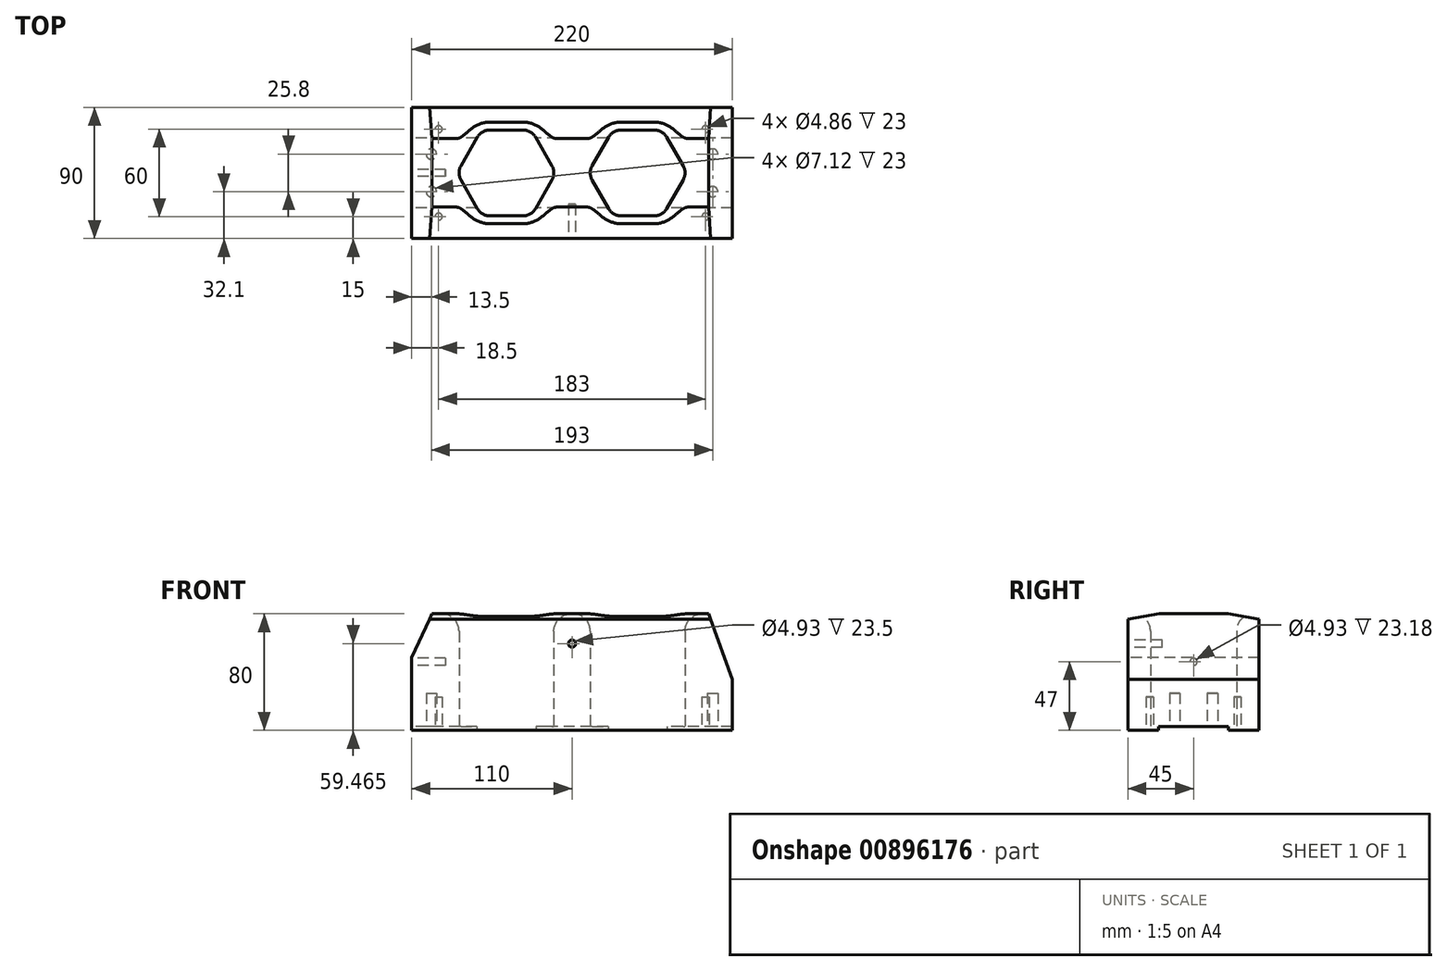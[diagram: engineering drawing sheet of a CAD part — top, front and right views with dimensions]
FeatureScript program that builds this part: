
annotation { "Feature Type Name" : "Feature", "Feature Type Description" : "" }
export const myFeature = defineFeature(function(context is Context, id is Id, definition is map)
    precondition{}
    {
        {
            var Q0;
            Q0=qCreatedBy(makeId("Top.planeOp"),FACE);
            var sketch = newSketch(context, id + "F0", { "sketchPlane" : qUnion([Q0])});
            skLineSegment(sketch, "E0.bottom", {"start": v(110, 45) * mm, "end": v(-110, 45) * mm});
            skLineSegment(sketch, "E0.top", {"start": v(110, -45) * mm, "end": v(-110, -45) * mm});
            skLineSegment(sketch, "E0.left", {"start": v(110, 45) * mm, "end": v(110, -45) * mm});
            skLineSegment(sketch, "E0.right", {"start": v(-110, 45) * mm, "end": v(-110, -45) * mm});
            skPoint(sketch, "E0.middle", {"position": v(0, 0) * mm});
            skSolve(sketch);
        }
        {
            var Q0;
            Q0=makeQuery(id+"F0.imprint","IMPRINT",FACE,{"disambiguationData":[TD([[makeQuery(id+"F0.imprint","IMPRINT",EDGE,{"derivedFrom":sQuery(id+"F0.wireOp",EDGE,"E0.bottom")}),1.0]])]});
            extrude(context, id + "F1", {"entities" : qUnion([Q0]), "depth" : 80 * mm, "offsetDistance" : 25 * mm});
        }
        {
            var Q0;
            {var subQ0=sQuery(id+"F0.wireOp",EDGE,"E0.top");var subQ1=sQuery(id+"F0.wireOp",EDGE,"E0.left");var subQ2=sQuery(id+"F0.wireOp",EDGE,"E0.right");Q0=makeQuery(id+"F8.boolean.opBoolean","SPLIT",FACE,{"disambiguationData":[TD([makeQuery(id+"F1.opExtrude","SWEPT_FACE",FACE,{"disambiguationData":[OSD([subQ0])]})])],"derivedFrom":makeQuery(id+"F1.opExtrude","CAP_FACE",FACE,{"disambiguationData":[OSD([sQuery(id+"F0.wireOp",EDGE,"E0.bottom"),subQ0,subQ1,subQ2])],"isStart":true})});}
            var sketch = newSketch(context, id + "F2", { "sketchPlane" : qUnion([Q0])});
            skLineSegment(sketch, "E1", {"start": v(0, 0) * mm, "end": v(45, 0) * mm});
            skLineSegment(sketch, "E2", {"start": v(0, 0) * mm, "end": v(-45, 0) * mm});
            skLineSegment(sketch, "E3", {"start": v(-45, 0) * mm, "end": v(-45, 29.5) * mm});
            skCircle(sketch, "E4.cCircle", {"center": v(-45, 0) * mm, "radius": 29.5 * mm, "construction": true});
            skLineSegment(sketch, "E4.0", {"start": v(-56.26, 29.5) * mm, "end": v(-33.74, 29.5) * mm});
            skLineSegment(sketch, "E4.1", {"start": v(-25.08, 24.5) * mm, "end": v(-13.82, 5) * mm});
            skLineSegment(sketch, "E4.2", {"start": v(-13.82, -5) * mm, "end": v(-25.08, -24.5) * mm});
            skLineSegment(sketch, "E4.3", {"start": v(-33.74, -29.5) * mm, "end": v(-56.26, -29.5) * mm});
            skLineSegment(sketch, "E4.4", {"start": v(-64.92, -24.5) * mm, "end": v(-76.18, -5) * mm});
            skLineSegment(sketch, "E4.5", {"start": v(-76.18, 5) * mm, "end": v(-64.92, 24.5) * mm});
            skPoint(sketch, "E4.0.midPoint", {"position": v(-45, 29.5) * mm});
            skLineSegment(sketch, "E5", {"start": v(45, 0) * mm, "end": v(45, 29.5) * mm});
            skCircle(sketch, "E6.cCircle", {"center": v(45, 0) * mm, "radius": 29.5 * mm, "construction": true});
            skLineSegment(sketch, "E6.0", {"start": v(33.74, 29.5) * mm, "end": v(56.26, 29.5) * mm});
            skLineSegment(sketch, "E6.1", {"start": v(64.92, 24.5) * mm, "end": v(76.18, 5) * mm});
            skLineSegment(sketch, "E6.2", {"start": v(76.18, -5) * mm, "end": v(64.92, -24.5) * mm});
            skLineSegment(sketch, "E6.3", {"start": v(56.26, -29.5) * mm, "end": v(33.74, -29.5) * mm});
            skLineSegment(sketch, "E6.4", {"start": v(25.08, -24.5) * mm, "end": v(13.82, -5) * mm});
            skLineSegment(sketch, "E6.5", {"start": v(13.82, 5) * mm, "end": v(25.08, 24.5) * mm});
            skPoint(sketch, "E6.0.midPoint", {"position": v(45, 29.5) * mm});
            skPoint(sketch, "E7.visualSharp", {"position": v(-62.03, 29.5) * mm});
            skArc(sketch, "E7.filletArc", {"start": v(-56.26, 29.5) * mm, "mid": v(-61.26, 28.16) * mm, "end": v(-64.92, 24.5) * mm});
            skPoint(sketch, "E8.visualSharp", {"position": v(-79.06, 0) * mm});
            skArc(sketch, "E8.filletArc", {"start": v(-76.18, 5) * mm, "mid": v(-77.52, 0) * mm, "end": v(-76.18, -5) * mm});
            skPoint(sketch, "E9.visualSharp", {"position": v(-62.03, -29.5) * mm});
            skArc(sketch, "E9.filletArc", {"start": v(-64.92, -24.5) * mm, "mid": v(-61.26, -28.16) * mm, "end": v(-56.26, -29.5) * mm});
            skPoint(sketch, "E10.visualSharp", {"position": v(-27.97, -29.5) * mm});
            skArc(sketch, "E10.filletArc", {"start": v(-33.74, -29.5) * mm, "mid": v(-28.74, -28.16) * mm, "end": v(-25.08, -24.5) * mm});
            skPoint(sketch, "E11.visualSharp", {"position": v(-10.94, 0) * mm});
            skArc(sketch, "E11.filletArc", {"start": v(-13.82, -5) * mm, "mid": v(-12.48, 0) * mm, "end": v(-13.82, 5) * mm});
            skPoint(sketch, "E12.visualSharp", {"position": v(-27.97, 29.5) * mm});
            skArc(sketch, "E12.filletArc", {"start": v(-25.08, 24.5) * mm, "mid": v(-28.74, 28.16) * mm, "end": v(-33.74, 29.5) * mm});
            skPoint(sketch, "E13.visualSharp", {"position": v(27.97, 29.5) * mm});
            skArc(sketch, "E13.filletArc", {"start": v(33.74, 29.5) * mm, "mid": v(28.74, 28.16) * mm, "end": v(25.08, 24.5) * mm});
            skPoint(sketch, "E14.visualSharp", {"position": v(10.94, 0) * mm});
            skArc(sketch, "E14.filletArc", {"start": v(13.82, 5) * mm, "mid": v(12.48, 0) * mm, "end": v(13.82, -5) * mm});
            skPoint(sketch, "E15.visualSharp", {"position": v(27.97, -29.5) * mm});
            skArc(sketch, "E15.filletArc", {"start": v(25.08, -24.5) * mm, "mid": v(28.74, -28.16) * mm, "end": v(33.74, -29.5) * mm});
            skPoint(sketch, "E16.visualSharp", {"position": v(62.03, -29.5) * mm});
            skArc(sketch, "E16.filletArc", {"start": v(56.26, -29.5) * mm, "mid": v(61.26, -28.16) * mm, "end": v(64.92, -24.5) * mm});
            skPoint(sketch, "E17.visualSharp", {"position": v(79.06, 0) * mm});
            skArc(sketch, "E17.filletArc", {"start": v(76.18, -5) * mm, "mid": v(77.52, 0) * mm, "end": v(76.18, 5) * mm});
            skPoint(sketch, "E18.visualSharp", {"position": v(62.03, 29.5) * mm});
            skArc(sketch, "E18.filletArc", {"start": v(64.92, 24.5) * mm, "mid": v(61.26, 28.16) * mm, "end": v(56.26, 29.5) * mm});
            skSolve(sketch);
        }
        {
            var Q0;
            {var subQ1=sQuery(id+"F2.wireOp",EDGE,"E4.2");Q0=makeQuery(id+"F2.imprint","IMPRINT",FACE,{"disambiguationData":[TD([[makeQuery(id+"F2.imprint","IMPRINT",EDGE,{"derivedFrom":subQ1}),-1.0]])]});}
            var Q1;
            {var subQ3=sQuery(id+"F2.wireOp",EDGE,"E2");var subQ7=sQuery(id+"F2.wireOp",EDGE,"E3");var subQ8=makeQuery(id+"F2.imprint","INTERSECT",VERTEX,{"derivedFrom":[subQ3,subQ7]});Q1=makeQuery(id+"F2.imprint","IMPRINT",FACE,{"disambiguationData":[TD([[makeQuery(id+"F2.imprint","IMPRINT",EDGE,{"disambiguationData":[TD([[subQ8,1.0]])],"derivedFrom":subQ3}),-1.0]])]});}
            var Q2;
            {var subQ0=sQuery(id+"F2.wireOp",EDGE,"E12.filletArc");Q2=makeQuery(id+"F2.imprint","IMPRINT",FACE,{"disambiguationData":[TD([[makeQuery(id+"F2.imprint","IMPRINT",EDGE,{"derivedFrom":subQ0}),1.0]])]});}
            var Q3;
            {var subQ0=sQuery(id+"F2.wireOp",EDGE,"E7.filletArc");Q3=makeQuery(id+"F2.imprint","IMPRINT",FACE,{"disambiguationData":[TD([[makeQuery(id+"F2.imprint","IMPRINT",EDGE,{"derivedFrom":subQ0}),1.0]])]});}
            var Q4;
            {var subQ0=sQuery(id+"F2.wireOp",EDGE,"E13.filletArc");Q4=makeQuery(id+"F2.imprint","IMPRINT",FACE,{"disambiguationData":[TD([[makeQuery(id+"F2.imprint","IMPRINT",EDGE,{"derivedFrom":subQ0}),1.0]])]});}
            var Q5;
            {var subQ0=sQuery(id+"F2.wireOp",EDGE,"E18.filletArc");Q5=makeQuery(id+"F2.imprint","IMPRINT",FACE,{"disambiguationData":[TD([[makeQuery(id+"F2.imprint","IMPRINT",EDGE,{"derivedFrom":subQ0}),1.0]])]});}
            var Q6;
            Q6=makeQuery(id+"F2.imprint","IMPRINT",FACE,{"disambiguationData":[TD([[makeQuery(id+"F2.imprint","IMPRINT",EDGE,{"derivedFrom":sQuery(id+"F2.wireOp",EDGE,"E6.2")}),-1.0]])]});
            var Q7;
            {var subQ3=sQuery(id+"F2.wireOp",EDGE,"E1");var subQ5=sQuery(id+"F2.wireOp",EDGE,"E5");var subQ6=makeQuery(id+"F2.imprint","INTERSECT",VERTEX,{"derivedFrom":[subQ3,subQ5]});Q7=makeQuery(id+"F2.imprint","IMPRINT",FACE,{"disambiguationData":[TD([[makeQuery(id+"F2.imprint","IMPRINT",EDGE,{"disambiguationData":[TD([[subQ6,1.0]])],"derivedFrom":subQ3}),1.0]])]});}
            extrude(context, id + "F3", {"entities" : qUnion([Q0, Q1, Q2, Q3, Q4, Q5, Q6, Q7]), "operationType" : NewBodyOperationType.REMOVE, "endBound" : BoundingType.THROUGH_ALL, "oppositeDirection" : true, "depth" : 25 * mm, "offsetDistance" : 25 * mm});
        }
        {
            var Q0;
            Q0=makeQuery(id+"F3.boolean.opBoolean","INTERSECT",EDGE,{"derivedFrom":[makeQuery(id+"F1.opExtrude","CAP_FACE",FACE,{"disambiguationData":[OSD([sQuery(id+"F0.wireOp",EDGE,"E0.bottom"),sQuery(id+"F0.wireOp",EDGE,"E0.top"),sQuery(id+"F0.wireOp",EDGE,"E0.left"),sQuery(id+"F0.wireOp",EDGE,"E0.right")])],"isStart":false}),makeQuery(id+"F3.opExtrude","SWEPT_FACE",FACE,{"disambiguationData":[OSD([sQuery(id+"F2.wireOp",EDGE,"E4.3")])]})]});
            var Q1;
            Q1=makeQuery(id+"F3.boolean.opBoolean","INTERSECT",EDGE,{"derivedFrom":[makeQuery(id+"F1.opExtrude","CAP_FACE",FACE,{"disambiguationData":[OSD([sQuery(id+"F0.wireOp",EDGE,"E0.bottom"),sQuery(id+"F0.wireOp",EDGE,"E0.top"),sQuery(id+"F0.wireOp",EDGE,"E0.left"),sQuery(id+"F0.wireOp",EDGE,"E0.right")])],"isStart":false}),makeQuery(id+"F3.opExtrude","SWEPT_FACE",FACE,{"disambiguationData":[OSD([sQuery(id+"F2.wireOp",EDGE,"E6.3")])]})]});
            fillet(context, id + "F4", {"entities" : qUnion([Q0, Q1]), "radius" : 12 * mm, "tangentPropagation" : true, "allowEdgeOverflow" : false});
        }
        {
            var Q0;
            Q0=makeQuery(id+"F1.opExtrude","SWEPT_FACE",FACE,{"disambiguationData":[OSD([sQuery(id+"F0.wireOp",EDGE,"E0.top")])]});
            var sketch = newSketch(context, id + "F5", { "sketchPlane" : qUnion([Q0])});
            skPoint(sketch, "E19.middle", {"position": v(0, 65.95) * mm});
            skPoint(sketch, "E20.orphan", {"position": v(0, 51.9) * mm});
            skPoint(sketch, "E21.end.orphan", {"position": v(0, 80) * mm});
            skPoint(sketch, "E22.top.end.orphan", {"position": v(-95, 50) * mm});
            skPoint(sketch, "E23.trimOffspring.start.orphan", {"position": v(95, 50) * mm});
            skLineSegment(sketch, "E24", {"start": v(-110, 50) * mm, "end": v(-96.01, 80) * mm});
            skLineSegment(sketch, "E25", {"start": v(-110, 80) * mm, "end": v(-110, 50) * mm});
            skLineSegment(sketch, "E26", {"start": v(110, 35) * mm, "end": v(93.62, 80) * mm});
            skLineSegment(sketch, "E27", {"start": v(110, 80) * mm, "end": v(110, 35) * mm});
            skLineSegment(sketch, "E28", {"start": v(0, 0) * mm, "end": v(0, 80) * mm});
            skLineSegment(sketch, "E29", {"start": v(110, 80) * mm, "end": v(93.62, 80) * mm});
            skLineSegment(sketch, "E30", {"start": v(-110, 80) * mm, "end": v(-96.01, 80) * mm});
            skSolve(sketch);
        }
        {
            var Q0;
            Q0=makeQuery(id+"F5.imprint","IMPRINT",FACE,{"disambiguationData":[TD([[makeQuery(id+"F5.imprint","IMPRINT",EDGE,{"derivedFrom":sQuery(id+"F5.wireOp",EDGE,"tVCkyzY6-PQv7-pjYg-ZoG2-eNGS0VEvuOqP")}),-1.0]])]});
            var Q1;
            Q1=makeQuery(id+"F5.imprint","IMPRINT",FACE,{"disambiguationData":[TD([[makeQuery(id+"F5.imprint","IMPRINT",EDGE,{"derivedFrom":sQuery(id+"F5.wireOp",EDGE,"MdysPOFG-TD7O-rCdf-9AqD-u6KUDIQ9QJOj")}),1.0]])]});
            var Q2;
            Q2=makeQuery(id+"F5.imprint","IMPRINT",FACE,{"disambiguationData":[TD([[makeQuery(id+"F5.imprint","IMPRINT",EDGE,{"derivedFrom":sQuery(id+"F5.wireOp",EDGE,"E24")}),1.0]])]});
            var Q3;
            Q3=makeQuery(id+"F5.imprint","IMPRINT",FACE,{"disambiguationData":[TD([[makeQuery(id+"F5.imprint","IMPRINT",EDGE,{"derivedFrom":sQuery(id+"F5.wireOp",EDGE,"E26")}),-1.0]])]});
            extrude(context, id + "F6", {"entities" : qUnion([Q0, Q1, Q2, Q3]), "operationType" : NewBodyOperationType.REMOVE, "oppositeDirection" : true, "depth" : 90 * mm, "offsetDistance" : 25 * mm});
        }
        {
            var Q0;
            Q0=makeQuery(id+"F1.opExtrude","SWEPT_FACE",FACE,{"disambiguationData":[OSD([sQuery(id+"F0.wireOp",EDGE,"E0.right")])]});
            var sketch = newSketch(context, id + "F7", { "sketchPlane" : qUnion([Q0])});
            skLineSegment(sketch, "E31", {"start": v(0, 0) * mm, "end": v(24, 0) * mm});
            skLineSegment(sketch, "E32", {"start": v(24, 0) * mm, "end": v(24, 2.5) * mm});
            skLineSegment(sketch, "E33", {"start": v(24, 2.5) * mm, "end": v(-24, 2.5) * mm});
            skLineSegment(sketch, "E34", {"start": v(-24, 2.5) * mm, "end": v(-24, 0) * mm});
            skLineSegment(sketch, "E35", {"start": v(-24, 0) * mm, "end": v(0, 0) * mm});
            skLineSegment(sketch, "E36", {"start": v(45, 78.17) * mm, "end": v(44.95, 78.17) * mm});
            skPoint(sketch, "E37.orphan", {"position": v(52.39, 80) * mm});
            skLineSegment(sketch, "E38.0", {"start": v(-45, 80) * mm, "end": v(-23.5, 80) * mm});
            skLineSegment(sketch, "E39", {"start": v(45, 76.2) * mm, "end": v(45, 80) * mm});
            skLineSegment(sketch, "E40", {"start": v(-45, 76.2) * mm, "end": v(-45, 80) * mm});
            skPoint(sketch, "E41.orphan", {"position": v(45.33, 80) * mm});
            skLineSegment(sketch, "E42", {"start": v(23.5, 80) * mm, "end": v(45, 76.2) * mm});
            skLineSegment(sketch, "E43", {"start": v(-23.5, 80) * mm, "end": v(-45, 76.2) * mm});
            skLineSegment(sketch, "E44.trimOffspring", {"start": v(23.5, 80) * mm, "end": v(45, 80) * mm});
            skPoint(sketch, "E45.start.orphan", {"position": v(0, 80) * mm});
            skSolve(sketch);
        }
        {
            var Q0;
            Q0=makeQuery(id+"F7.imprint","IMPRINT",FACE,{"disambiguationData":[TD([[makeQuery(id+"F7.imprint","IMPRINT",EDGE,{"derivedFrom":sQuery(id+"F7.wireOp",EDGE,"E38.0")}),-1.0]])]});
            var Q1;
            {var subQ2=sQuery(id+"F7.wireOp",EDGE,"E42");Q1=makeQuery(id+"F7.imprint","IMPRINT",FACE,{"disambiguationData":[TD([[makeQuery(id+"F7.imprint","IMPRINT",EDGE,{"derivedFrom":subQ2}),1.0]])]});}
            var Q2;
            Q2=makeQuery(id+"F7.imprint","IMPRINT",FACE,{"disambiguationData":[TD([[makeQuery(id+"F7.imprint","IMPRINT",EDGE,{"derivedFrom":sQuery(id+"F7.wireOp",EDGE,"E31")}),1.0]])]});
            extrude(context, id + "F8", {"entities" : qUnion([Q0, Q1, Q2]), "operationType" : NewBodyOperationType.REMOVE, "endBound" : BoundingType.THROUGH_ALL, "oppositeDirection" : true, "depth" : 25 * mm, "offsetDistance" : 25 * mm});
        }
        {
            var Q0;
            Q0=makeQuery(id+"F1.opExtrude","SWEPT_FACE",FACE,{"disambiguationData":[OSD([sQuery(id+"F0.wireOp",EDGE,"E0.right")])]});
            var sketch = newSketch(context, id + "F9", { "sketchPlane" : qUnion([Q0])});
            skCircle(sketch, "E46", {"center": v(0, 47) * mm, "radius": 2.46 * mm});
            skSolve(sketch);
        }
        {
            var Q0;
            Q0=makeQuery(id+"F9.imprint","IMPRINT",FACE,{"disambiguationData":[TD([[makeQuery(id+"F9.imprint","IMPRINT",EDGE,{"derivedFrom":sQuery(id+"F9.wireOp",EDGE,"E46")}),1.0]])]});
            extrude(context, id + "F10", {"entities" : qUnion([Q0]), "operationType" : NewBodyOperationType.REMOVE, "oppositeDirection" : true, "depth" : 23.18 * mm, "offsetDistance" : 25 * mm});
        }
        {
            var Q0;
            Q0=makeQuery(id+"F1.opExtrude","SWEPT_FACE",FACE,{"disambiguationData":[OSD([sQuery(id+"F0.wireOp",EDGE,"E0.top")])]});
            var sketch = newSketch(context, id + "F11", { "sketchPlane" : qUnion([Q0])});
            skCircle(sketch, "E47", {"center": v(0, 59.47) * mm, "radius": 2.46 * mm});
            skSolve(sketch);
        }
        {
            var Q0;
            Q0=makeQuery(id+"F11.imprint","IMPRINT",FACE,{"disambiguationData":[TD([[makeQuery(id+"F11.imprint","IMPRINT",EDGE,{"derivedFrom":sQuery(id+"F11.wireOp",EDGE,"E47")}),1.0]])]});
            extrude(context, id + "F12", {"entities" : qUnion([Q0]), "operationType" : NewBodyOperationType.REMOVE, "oppositeDirection" : true, "depth" : 23.5 * mm, "offsetDistance" : 25 * mm});
        }
        {
            var Q0;
            {var subQ0=sQuery(id+"F0.wireOp",EDGE,"E0.top");var subQ1=sQuery(id+"F0.wireOp",EDGE,"E0.left");var subQ2=sQuery(id+"F0.wireOp",EDGE,"E0.right");Q0=makeQuery(id+"F8.boolean.opBoolean","SPLIT",FACE,{"disambiguationData":[TD([makeQuery(id+"F1.opExtrude","SWEPT_FACE",FACE,{"disambiguationData":[OSD([subQ0])]})])],"derivedFrom":makeQuery(id+"F1.opExtrude","CAP_FACE",FACE,{"disambiguationData":[OSD([sQuery(id+"F0.wireOp",EDGE,"E0.bottom"),subQ0,subQ1,subQ2])],"isStart":true})});}
            var sketch = newSketch(context, id + "F13", { "sketchPlane" : qUnion([Q0])});
            skPoint(sketch, "E48.startSnap0", {"position": v(-96.5, -0.05) * mm});
            skPoint(sketch, "E49.orphan", {"position": v(-96.5, -45.1) * mm});
            skPoint(sketch, "E50.orphan", {"position": v(-96.5, 45) * mm});
            skCircle(sketch, "E51", {"center": v(-91.5, 30) * mm, "radius": 2.43 * mm});
            skCircle(sketch, "E52", {"center": v(-96.5, 12.9) * mm, "radius": 3.56 * mm});
            skCircle(sketch, "E53", {"center": v(-96.5, -12.9) * mm, "radius": 3.56 * mm});
            skCircle(sketch, "E54", {"center": v(-91.5, -30) * mm, "radius": 2.43 * mm});
            skCircle(sketch, "E55", {"center": v(91.5, -30) * mm, "radius": 2.43 * mm});
            skCircle(sketch, "E56", {"center": v(96.5, -12.9) * mm, "radius": 3.56 * mm});
            skCircle(sketch, "E57", {"center": v(96.5, 12.9) * mm, "radius": 3.56 * mm});
            skCircle(sketch, "E58", {"center": v(91.5, 30) * mm, "radius": 2.43 * mm});
            skSolve(sketch);
        }
        {
            var Q0;
            Q0=makeQuery(id+"F13.imprint","IMPRINT",FACE,{"disambiguationData":[TD([[makeQuery(id+"F13.imprint","IMPRINT",EDGE,{"derivedFrom":sQuery(id+"F13.wireOp",EDGE,"E51")}),1.0]])]});
            var Q1;
            Q1=makeQuery(id+"F13.imprint","IMPRINT",FACE,{"disambiguationData":[TD([[makeQuery(id+"F13.imprint","IMPRINT",EDGE,{"derivedFrom":sQuery(id+"F13.wireOp",EDGE,"E58")}),1.0]])]});
            var Q2;
            Q2=makeQuery(id+"F13.imprint","IMPRINT",FACE,{"disambiguationData":[TD([[makeQuery(id+"F13.imprint","IMPRINT",EDGE,{"derivedFrom":sQuery(id+"F13.wireOp",EDGE,"E55")}),1.0]])]});
            var Q3;
            Q3=makeQuery(id+"F13.imprint","IMPRINT",FACE,{"disambiguationData":[TD([[makeQuery(id+"F13.imprint","IMPRINT",EDGE,{"derivedFrom":sQuery(id+"F13.wireOp",EDGE,"E54")}),1.0]])]});
            extrude(context, id + "F14", {"entities" : qUnion([Q0, Q1, Q2, Q3]), "operationType" : NewBodyOperationType.REMOVE, "oppositeDirection" : true, "depth" : 23 * mm, "offsetDistance" : 25 * mm});
        }
        {
            var Q0;
            Q0=makeQuery(id+"F13.imprint","IMPRINT",FACE,{"disambiguationData":[TD([[makeQuery(id+"F13.imprint","IMPRINT",EDGE,{"derivedFrom":sQuery(id+"F13.wireOp",EDGE,"E52")}),1.0]])]});
            var Q1;
            Q1=makeQuery(id+"F13.imprint","IMPRINT",FACE,{"disambiguationData":[TD([[makeQuery(id+"F13.imprint","IMPRINT",EDGE,{"derivedFrom":sQuery(id+"F13.wireOp",EDGE,"E53")}),1.0]])]});
            var Q2;
            Q2=makeQuery(id+"F13.imprint","IMPRINT",FACE,{"disambiguationData":[TD([[makeQuery(id+"F13.imprint","IMPRINT",EDGE,{"derivedFrom":sQuery(id+"F13.wireOp",EDGE,"E56")}),1.0]])]});
            var Q3;
            Q3=makeQuery(id+"F13.imprint","IMPRINT",FACE,{"disambiguationData":[TD([[makeQuery(id+"F13.imprint","IMPRINT",EDGE,{"derivedFrom":sQuery(id+"F13.wireOp",EDGE,"E57")}),1.0]])]});
            extrude(context, id + "F15", {"entities" : qUnion([Q0, Q1, Q2, Q3]), "operationType" : NewBodyOperationType.REMOVE, "oppositeDirection" : true, "depth" : 25.5 * mm, "offsetDistance" : 25 * mm});
        }
    });
